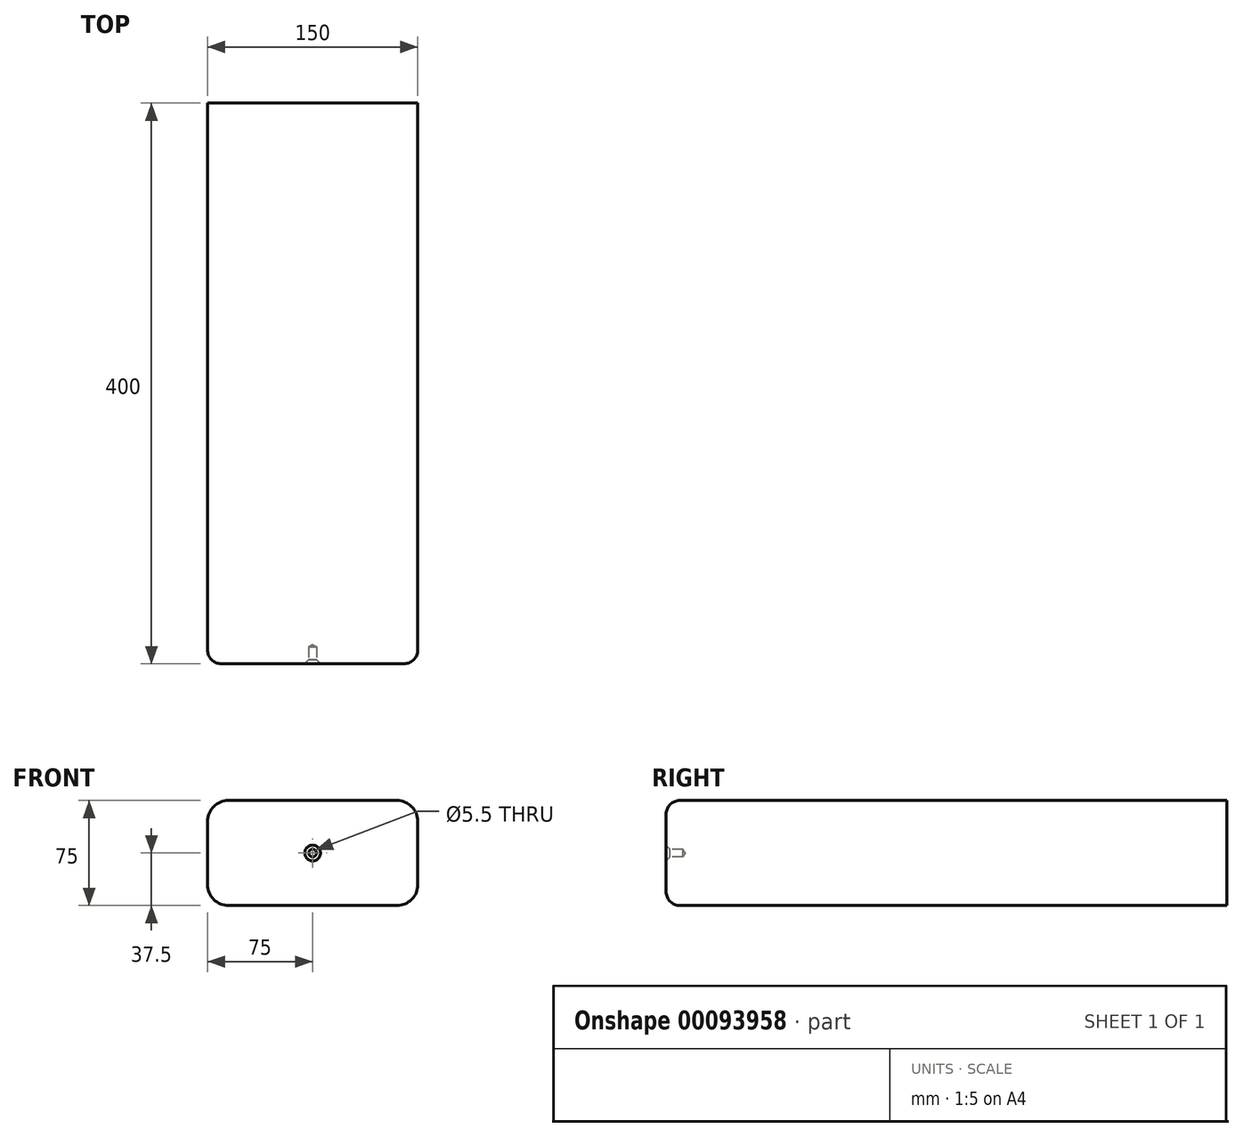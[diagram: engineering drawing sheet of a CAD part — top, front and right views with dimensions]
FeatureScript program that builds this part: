
annotation { "Feature Type Name" : "Feature", "Feature Type Description" : "" }
export const myFeature = defineFeature(function(context is Context, id is Id, definition is map)
    precondition{}
    {
        {
            var Q0;
            Q0=qCreatedBy(makeId("Front.planeOp"),FACE);
            var sketch = newSketch(context, id + "F0", { "sketchPlane" : qUnion([Q0])});
            skLineSegment(sketch, "E0.bottom", {"start": v(-75, 37.5) * mm, "end": v(75, 37.5) * mm});
            skLineSegment(sketch, "E0.top", {"start": v(-75, -37.5) * mm, "end": v(75, -37.5) * mm});
            skLineSegment(sketch, "E0.left", {"start": v(-75, 37.5) * mm, "end": v(-75, -37.5) * mm});
            skLineSegment(sketch, "E0.right", {"start": v(75, 37.5) * mm, "end": v(75, -37.5) * mm});
            skLineSegment(sketch, "E1", {"start": v(0, -69.24) * mm, "end": v(0, 71.38) * mm, "construction": true});
            skLineSegment(sketch, "E2", {"start": v(-95.9, 0) * mm, "end": v(93.75, 0) * mm, "construction": true});
            skSolve(sketch);
        }
        {
            var Q0;
            Q0 = qSketchRegion(id + "F0", true);
            extrude(context, id + "F1", {"entities" : qUnion([Q0]), "depth" : 400 * mm});
        }
        {
            var Q0;
            Q0=makeQuery(id+"F1.opExtrude","SWEPT_EDGE",EDGE,{"disambiguationData":[OSD([sQuery(id+"F0.wireOp",EDGE,"E0.bottom"),sQuery(id+"F0.wireOp",EDGE,"E0.right")])]});
            var Q1;
            Q1=makeQuery(id+"F1.opExtrude","SWEPT_EDGE",EDGE,{"disambiguationData":[OSD([sQuery(id+"F0.wireOp",EDGE,"E0.top"),sQuery(id+"F0.wireOp",EDGE,"E0.right")])]});
            var Q2;
            Q2=makeQuery(id+"F1.opExtrude","SWEPT_EDGE",EDGE,{"disambiguationData":[OSD([sQuery(id+"F0.wireOp",EDGE,"E0.bottom"),sQuery(id+"F0.wireOp",EDGE,"E0.left")])]});
            var Q3;
            Q3=makeQuery(id+"F1.opExtrude","SWEPT_EDGE",EDGE,{"disambiguationData":[OSD([sQuery(id+"F0.wireOp",EDGE,"E0.top"),sQuery(id+"F0.wireOp",EDGE,"E0.left")])]});
            fillet(context, id + "F2", {"entities" : qUnion([Q0, Q1, Q2, Q3]), "radius" : 15 * mm, "tangentPropagation" : true, "allowEdgeOverflow" : false});
        }
        {
            var Q0;
            Q0=makeQuery(id+"F1.opExtrude","CAP_FACE",FACE,{"disambiguationData":[OSD([sQuery(id+"F0.wireOp",EDGE,"E0.bottom"),sQuery(id+"F0.wireOp",EDGE,"E0.top"),sQuery(id+"F0.wireOp",EDGE,"E0.left"),sQuery(id+"F0.wireOp",EDGE,"E0.right")])],"isStart":false});
            var sketch = newSketch(context, id + "F3", { "sketchPlane" : qUnion([Q0])});
            skPoint(sketch, "E3", {"position": v(0, 0) * mm});
            skSolve(sketch);
        }
        {
            var Q0;
            Q0=sQuery(id+"F3.wireOp",VERTEX,"E3");
            var Q1;
            Q1=makeQuery(id+"F1.opExtrude","SWEPT_BODY",BODY,{"disambiguationData":[OSD([sQuery(id+"F0.wireOp",EDGE,"E0.bottom"),sQuery(id+"F0.wireOp",EDGE,"E0.top"),sQuery(id+"F0.wireOp",EDGE,"E0.left"),sQuery(id+"F0.wireOp",EDGE,"E0.right")])]});
            hole(context, id + "F4", {"style" : HoleStyle.C_SINK, "endStyle" : HoleEndStyle.BLIND, "standardTappedOrClearance" : lookupTablePath({ "standard" : "ISO", "fit" : "Normal", "size" : "M5", "type" : "Clearance" }), "standardBlindInLast" : lookupTablePath({ "fit" : "Standard", "standard" : "ISO", "size" : "M5", "type" : "Clearance" }), "holeDiameter" : 5.5 * mm, "cSinkDiameter" : 11.2 * mm, "cSinkAngle" : 90 * degree, "holeDepth" : 12 * mm, "startFromSketch" : true, "locations" : qUnion([Q0]), "scope" : qUnion([Q1])});
        }
        {
            var Q0;
            Q0=makeQuery(id+"F1.opExtrude","CAP_EDGE",EDGE,{"disambiguationData":[OSD([sQuery(id+"F0.wireOp",EDGE,"E0.bottom")])],"isStart":false});
            fillet(context, id + "F5", {"entities" : qUnion([Q0]), "radius" : 10 * mm, "tangentPropagation" : true, "allowEdgeOverflow" : false});
        }
    });
